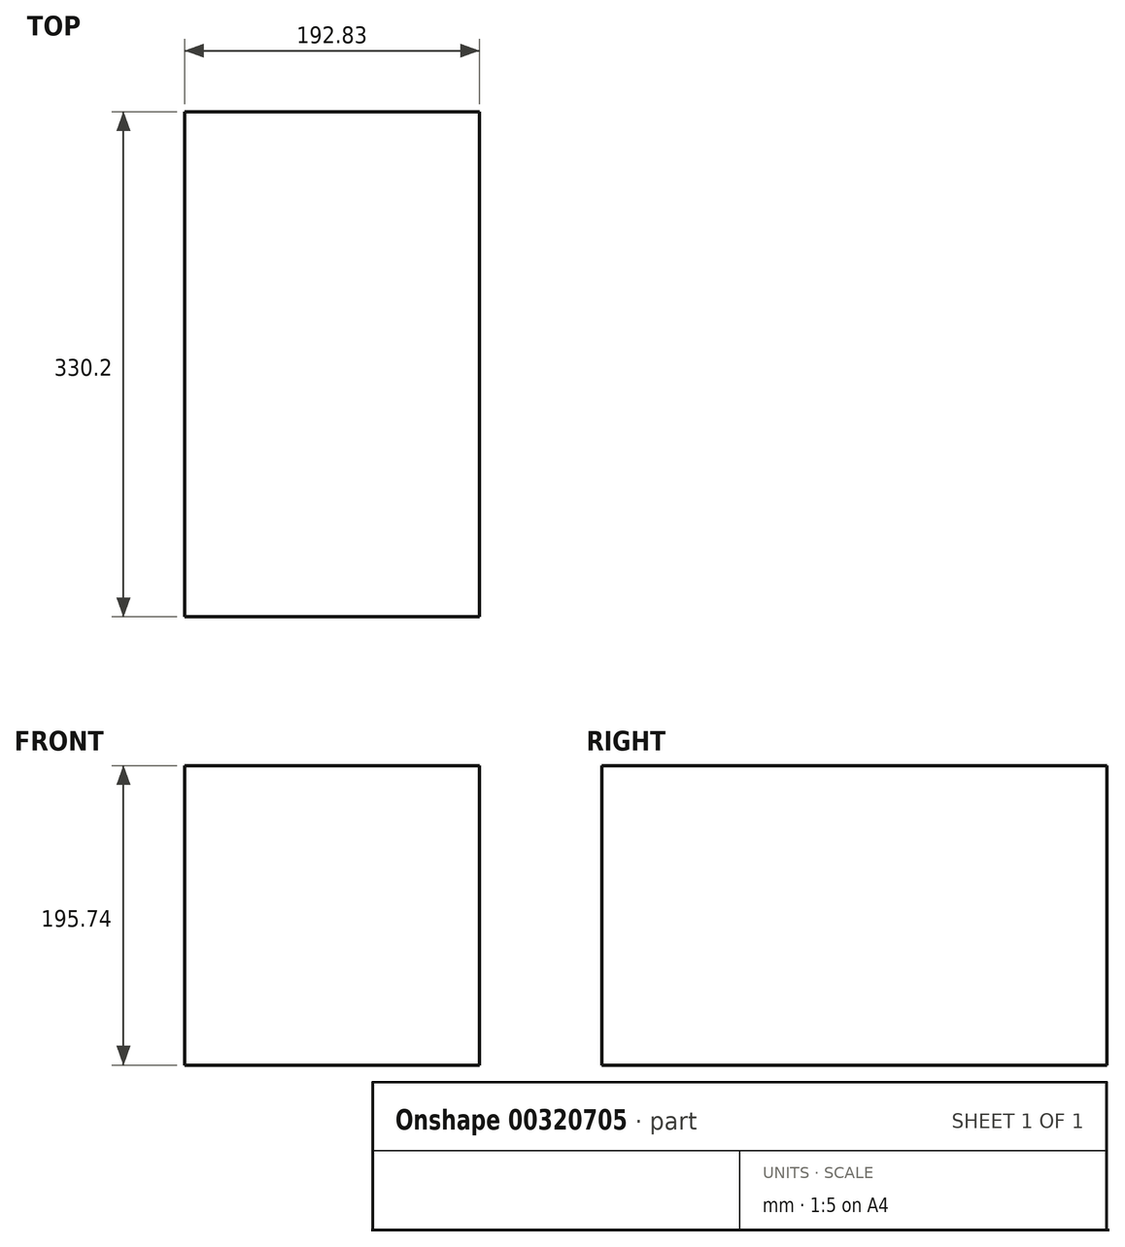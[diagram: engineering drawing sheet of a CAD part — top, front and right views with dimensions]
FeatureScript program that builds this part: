
annotation { "Feature Type Name" : "Feature", "Feature Type Description" : "" }
export const myFeature = defineFeature(function(context is Context, id is Id, definition is map)
    precondition{}
    {
        {
            var Q0;
            Q0=qCreatedBy(makeId("Front.planeOp"),FACE);
            var sketch = newSketch(context, id + "F0", { "sketchPlane" : qUnion([Q0])});
            skLineSegment(sketch, "E0.bottom", {"start": v(-96.18, 96.75) * mm, "end": v(96.65, 96.75) * mm});
            skLineSegment(sketch, "E0.top", {"start": v(-96.18, -98.99) * mm, "end": v(96.65, -98.99) * mm});
            skLineSegment(sketch, "E0.left", {"start": v(-96.18, 96.75) * mm, "end": v(-96.18, -98.99) * mm});
            skLineSegment(sketch, "E0.right", {"start": v(96.65, 96.75) * mm, "end": v(96.65, -98.99) * mm});
            skSolve(sketch);
        }
        {
            var Q0;
            Q0=makeQuery(id+"F0.imprint","IMPRINT",FACE,{"disambiguationData":[TD([[makeQuery(id+"F0.imprint","IMPRINT",EDGE,{"derivedFrom":sQuery(id+"F0.wireOp",EDGE,"E0.bottom")}),-1.0]])]});
            extrude(context, id + "F1", {"entities" : qUnion([Q0]), "oppositeDirection" : true, "depth" : 330.2 * mm});
        }
    });
